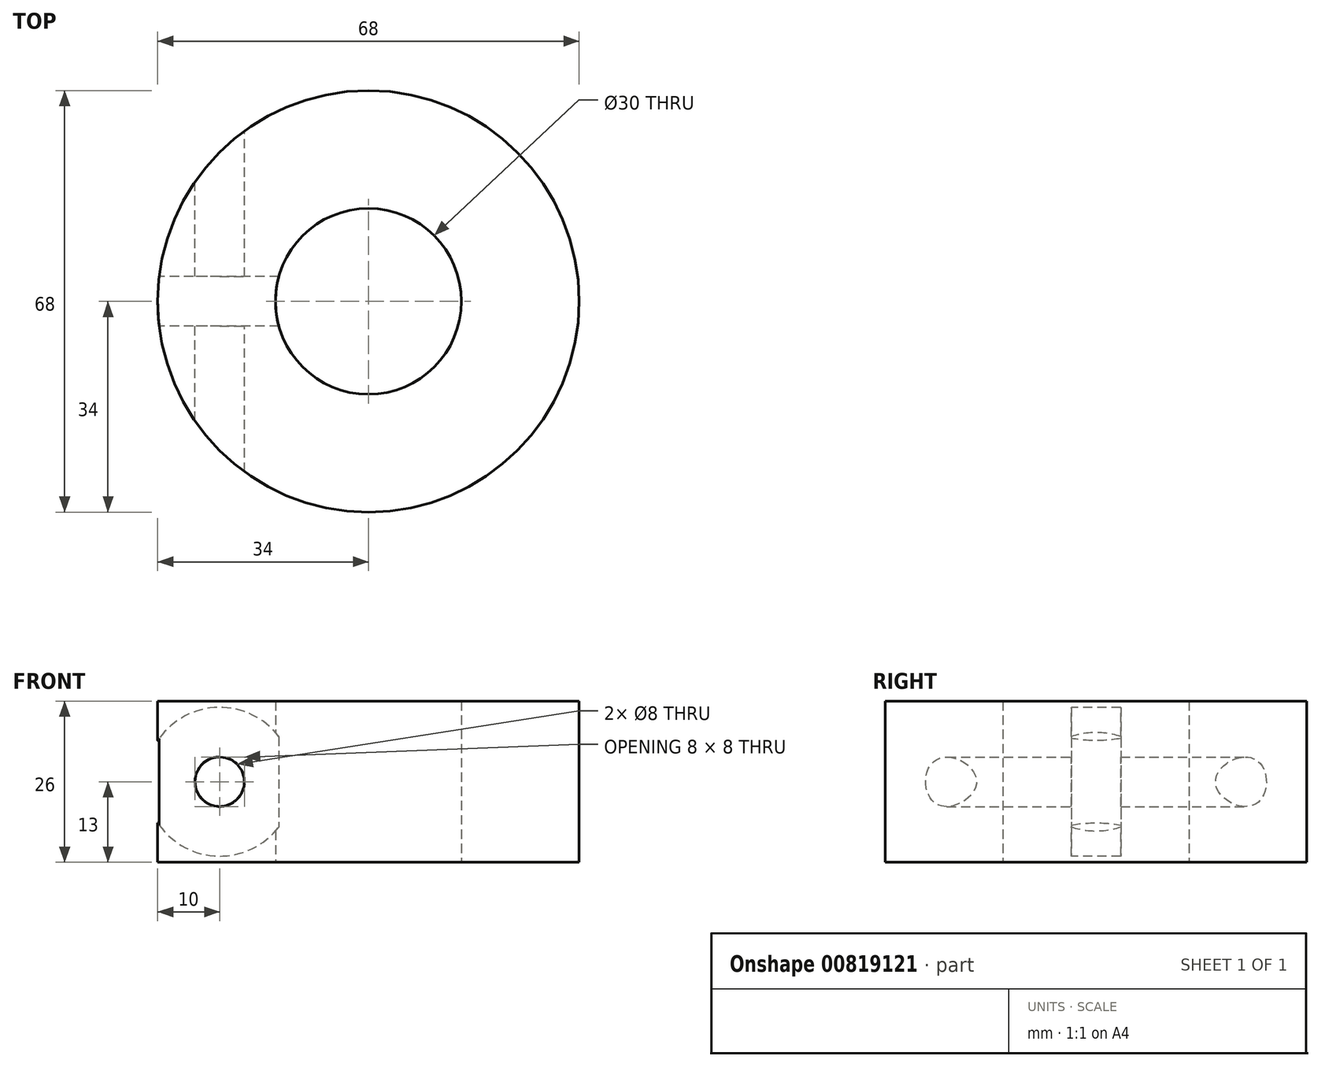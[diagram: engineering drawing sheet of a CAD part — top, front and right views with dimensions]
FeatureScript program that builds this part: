
annotation { "Feature Type Name" : "Feature", "Feature Type Description" : "" }
export const myFeature = defineFeature(function(context is Context, id is Id, definition is map)
    precondition{}
    {
        {
            var Q0;
            Q0=qCreatedBy(makeId("Top.planeOp"),FACE);
            var sketch = newSketch(context, id + "F0", { "sketchPlane" : qUnion([Q0])});
            skCircle(sketch, "E0", {"center": v(0, 0) * mm, "radius": 34 * mm});
            skCircle(sketch, "E1", {"center": v(0, 0) * mm, "radius": 15 * mm});
            skSolve(sketch);
        }
        {
            var Q0;
            Q0=makeQuery(id+"F0.imprint","IMPRINT",FACE,{"disambiguationData":[TD([[makeQuery(id+"F0.imprint","IMPRINT",EDGE,{"derivedFrom":sQuery(id+"F0.wireOp",EDGE,"E0")}),1.0]])]});
            extrude(context, id + "F1", {"entities" : qUnion([Q0]), "depth" : 26 * mm, "offsetDistance" : 25 * mm});
        }
        {
            var Q0;
            Q0=qCreatedBy(makeId("Front.planeOp"),FACE);
            var sketch = newSketch(context, id + "F2", { "sketchPlane" : qUnion([Q0])});
            skLineSegment(sketch, "E2", {"start": v(-24, 0) * mm, "end": v(-24, 26) * mm, "construction": true});
            skLineSegment(sketch, "E3", {"start": v(-35, 23.7) * mm, "end": v(-35, 2.12) * mm, "construction": true});
            skCircle(sketch, "E4", {"center": v(-24, 13) * mm, "radius": 12 * mm});
            skLineSegment(sketch, "E5", {"start": v(0, 0) * mm, "end": v(0, 28.53) * mm, "construction": true});
            skSolve(sketch);
        }
        {
            var Q0;
            Q0=makeQuery(id+"F2.imprint","IMPRINT",FACE,{"disambiguationData":[TD([[makeQuery(id+"F2.imprint","IMPRINT",EDGE,{"derivedFrom":sQuery(id+"F2.wireOp",EDGE,"E4")}),1.0]])]});
            extrude(context, id + "F3", {"entities" : qUnion([Q0]), "operationType" : NewBodyOperationType.REMOVE, "oppositeDirection" : true, "depth" : 4 * mm, "offsetDistance" : 25 * mm, "hasSecondDirection" : true, "secondDirectionOppositeDirection" : false, "secondDirectionDepth" : 4 * mm});
        }
        {
            var Q0;
            Q0=qCreatedBy(makeId("Front.planeOp"),FACE);
            var sketch = newSketch(context, id + "F4", { "sketchPlane" : qUnion([Q0])});
            skCircle(sketch, "E6", {"center": v(-24, 13) * mm, "radius": 4 * mm});
            skSolve(sketch);
        }
        {
            var Q0;
            Q0 = qSketchRegion(id + "F4", true);
            extrude(context, id + "F5", {"entities" : qUnion([Q0]), "operationType" : NewBodyOperationType.REMOVE, "endBound" : BoundingType.THROUGH_ALL, "depth" : 25 * mm, "offsetDistance" : 25 * mm, "hasSecondDirection" : true, "secondDirectionBound" : SecondDirectionBoundingType.THROUGH_ALL, "secondDirectionOppositeDirection" : true, "secondDirectionDepth" : 25 * mm});
        }
    });
